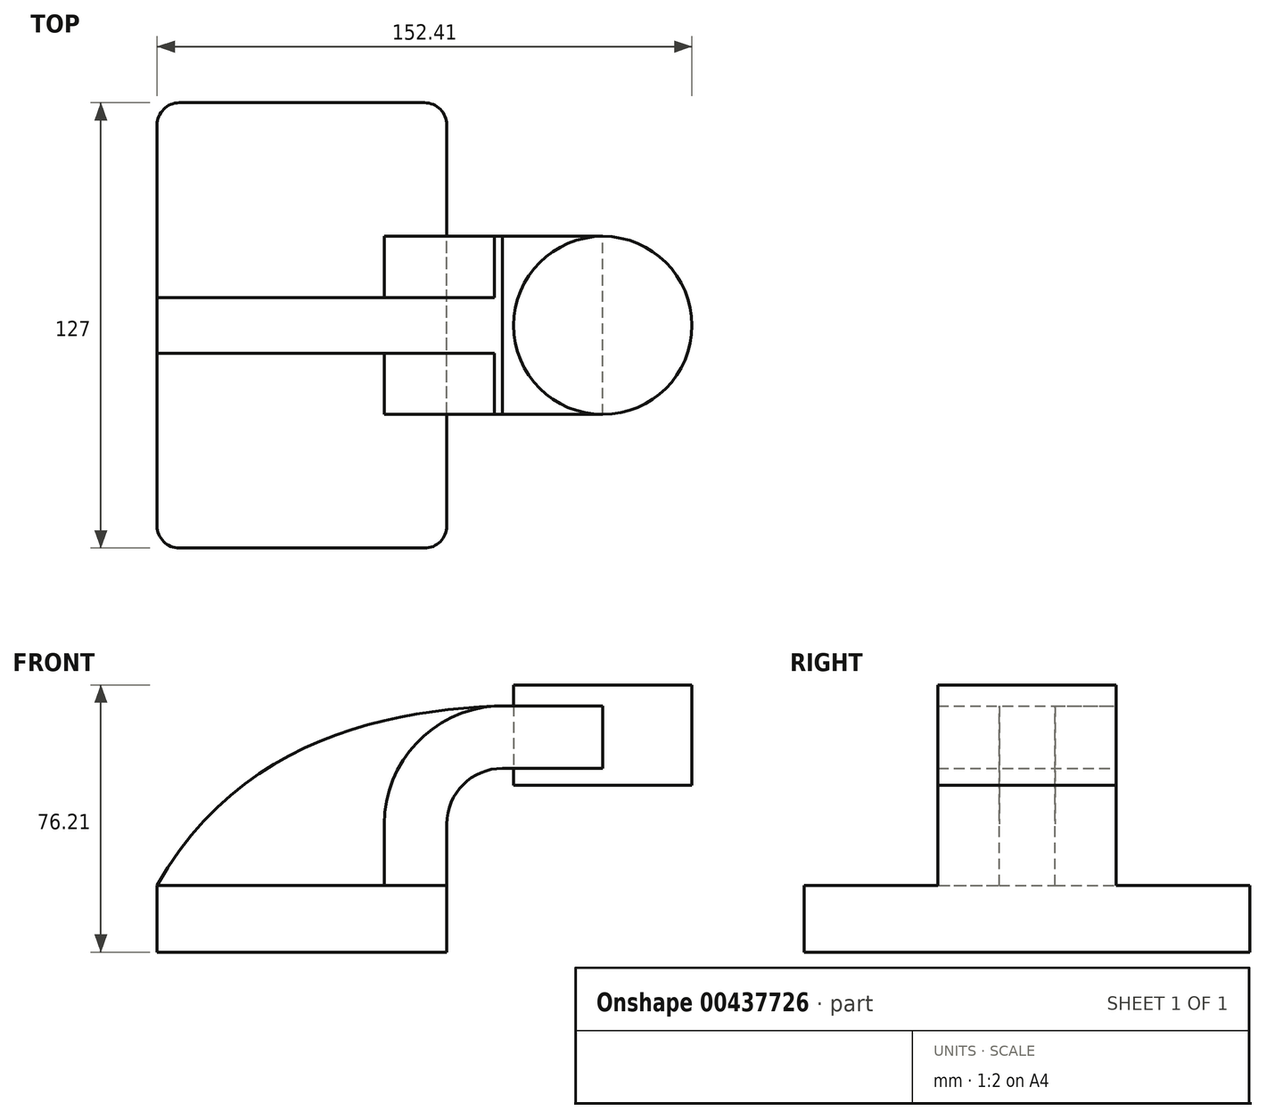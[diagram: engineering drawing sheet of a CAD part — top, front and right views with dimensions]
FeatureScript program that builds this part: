
annotation { "Feature Type Name" : "Feature", "Feature Type Description" : "" }
export const myFeature = defineFeature(function(context is Context, id is Id, definition is map)
    precondition{}
    {
        {
            var Q0;
            Q0=qCreatedBy(makeId("Front.planeOp"),FACE);
            var sketch = newSketch(context, id + "F0", { "sketchPlane" : qUnion([Q0])});
            skLineSegment(sketch, "E0.bottom", {"start": v(41.27, 9.53) * mm, "end": v(-41.28, 9.53) * mm});
            skLineSegment(sketch, "E0.top", {"start": v(41.28, -9.52) * mm, "end": v(-41.27, -9.52) * mm});
            skLineSegment(sketch, "E0.left", {"start": v(41.28, 9.53) * mm, "end": v(41.28, -9.52) * mm});
            skLineSegment(sketch, "E0.right", {"start": v(-41.28, 9.53) * mm, "end": v(-41.28, -9.52) * mm});
            skPoint(sketch, "E0.middle", {"position": v(0, 0) * mm});
            skLineSegment(sketch, "E1.bottom", {"start": v(111.12, 38.1) * mm, "end": v(60.32, 38.1) * mm});
            skLineSegment(sketch, "E1.top", {"start": v(111.12, 66.68) * mm, "end": v(60.32, 66.68) * mm});
            skLineSegment(sketch, "E1.left", {"start": v(111.12, 38.1) * mm, "end": v(111.12, 66.68) * mm});
            skLineSegment(sketch, "E1.right", {"start": v(60.32, 38.1) * mm, "end": v(60.32, 66.68) * mm});
            skPoint(sketch, "E1.middle", {"position": v(85.72, 52.39) * mm});
            skLineSegment(sketch, "E2", {"start": v(41.27, 9.53) * mm, "end": v(41.27, 27) * mm});
            skArc(sketch, "E3", {"start": v(41.27, 27) * mm, "mid": v(45.92, 38.23) * mm, "end": v(57.15, 42.88) * mm});
            skLineSegment(sketch, "E4", {"start": v(57.15, 42.88) * mm, "end": v(85.72, 42.88) * mm});
            skLineSegment(sketch, "E5.0", {"start": v(57.15, 60.67) * mm, "end": v(85.72, 60.67) * mm});
            skArc(sketch, "E5.1", {"start": v(23.48, 27) * mm, "mid": v(33.34, 50.81) * mm, "end": v(57.15, 60.67) * mm});
            skLineSegment(sketch, "E5.2", {"start": v(23.48, 9.53) * mm, "end": v(23.48, 27) * mm});
            skLineSegment(sketch, "E6", {"start": v(85.72, 38.1) * mm, "end": v(85.73, 66.68) * mm});
            skFitSpline(sketch, "E7", {"points": [v(-41.28, 9.53) * mm, v(57.15, 60.67) * mm], "startDerivative": vector(69.67, 123.76) * mm, "endDerivative": vector(99.93, 2.85) * mm});
            skSolve(sketch);
        }
        {
            var Q0;
            Q0=makeQuery(id+"F0.imprint","IMPRINT",FACE,{"disambiguationData":[TD([[makeQuery(id+"F0.imprint","IMPRINT",EDGE,{"derivedFrom":sQuery(id+"F0.wireOp",EDGE,"E0.top")}),-1.0]])]});
            extrude(context, id + "F1", {"entities" : qUnion([Q0]), "endBound" : BoundingType.SYMMETRIC, "depth" : 127 * mm});
        }
        {
            var Q0;
            {var subQ1=sQuery(id+"F0.wireOp",EDGE,"E2");Q0=makeQuery(id+"F0.imprint","IMPRINT",FACE,{"disambiguationData":[TD([[makeQuery(id+"F0.imprint","IMPRINT",EDGE,{"derivedFrom":subQ1}),1.0]])]});}
            var Q1;
            {var subQ0=sQuery(id+"F0.wireOp",EDGE,"E4");var subQ1=sQuery(id+"F0.wireOp",EDGE,"E1.right");var subQ2=makeQuery(id+"F0.imprint","INTERSECT",VERTEX,{"derivedFrom":[subQ1,subQ0]});Q1=makeQuery(id+"F0.imprint","IMPRINT",FACE,{"disambiguationData":[TD([[makeQuery(id+"F0.imprint","IMPRINT",EDGE,{"disambiguationData":[TD([[subQ2,-1.0]])],"derivedFrom":subQ1}),-1.0]])]});}
            extrude(context, id + "F2", {"entities" : qUnion([Q0, Q1]), "operationType" : NewBodyOperationType.ADD, "endBound" : BoundingType.SYMMETRIC, "depth" : 50.8 * mm});
        }
        {
            var Q0;
            {var subQ3=sQuery(id+"F0.wireOp",EDGE,"E5.2");Q0=makeQuery(id+"F0.imprint","IMPRINT",FACE,{"disambiguationData":[TD([[makeQuery(id+"F0.imprint","IMPRINT",EDGE,{"derivedFrom":subQ3}),1.0]])]});}
            extrude(context, id + "F3", {"entities" : qUnion([Q0]), "operationType" : NewBodyOperationType.ADD, "endBound" : BoundingType.SYMMETRIC, "depth" : 15.88 * mm});
        }
        {
            var Q0;
            {var subQ0=sQuery(id+"F0.wireOp",EDGE,"E1.left");Q0=makeQuery(id+"F0.imprint","IMPRINT",FACE,{"disambiguationData":[TD([[makeQuery(id+"F0.imprint","IMPRINT",EDGE,{"derivedFrom":subQ0}),1.0]])]});}
            var Q1;
            Q1=sQuery(id+"F0.wireOp",EDGE,"E6");
            revolve(context, id + "F4", {"entities" : qUnion([Q0]), "axis" : qUnion([Q1]), "revolveType" : RevolveType.FULL});
        }
        {
            var Q0;
            Q0=makeQuery(id+"F1.opExtrude","CAP_EDGE",EDGE,{"disambiguationData":[OSD([sQuery(id+"F0.wireOp",EDGE,"E0.left")])],"isStart":false});
            var Q1;
            Q1=makeQuery(id+"F1.opExtrude","CAP_EDGE",EDGE,{"disambiguationData":[OSD([sQuery(id+"F0.wireOp",EDGE,"E0.right")])],"isStart":false});
            var Q2;
            Q2=makeQuery(id+"F1.opExtrude","CAP_EDGE",EDGE,{"disambiguationData":[OSD([sQuery(id+"F0.wireOp",EDGE,"E0.left")])],"isStart":true});
            var Q3;
            Q3=makeQuery(id+"F1.opExtrude","CAP_EDGE",EDGE,{"disambiguationData":[OSD([sQuery(id+"F0.wireOp",EDGE,"E0.right")])],"isStart":true});
            fillet(context, id + "F5", {"entities" : qUnion([Q0, Q1, Q2, Q3]), "radius" : 6.35 * mm, "tangentPropagation" : true, "allowEdgeOverflow" : false});
        }
    });
